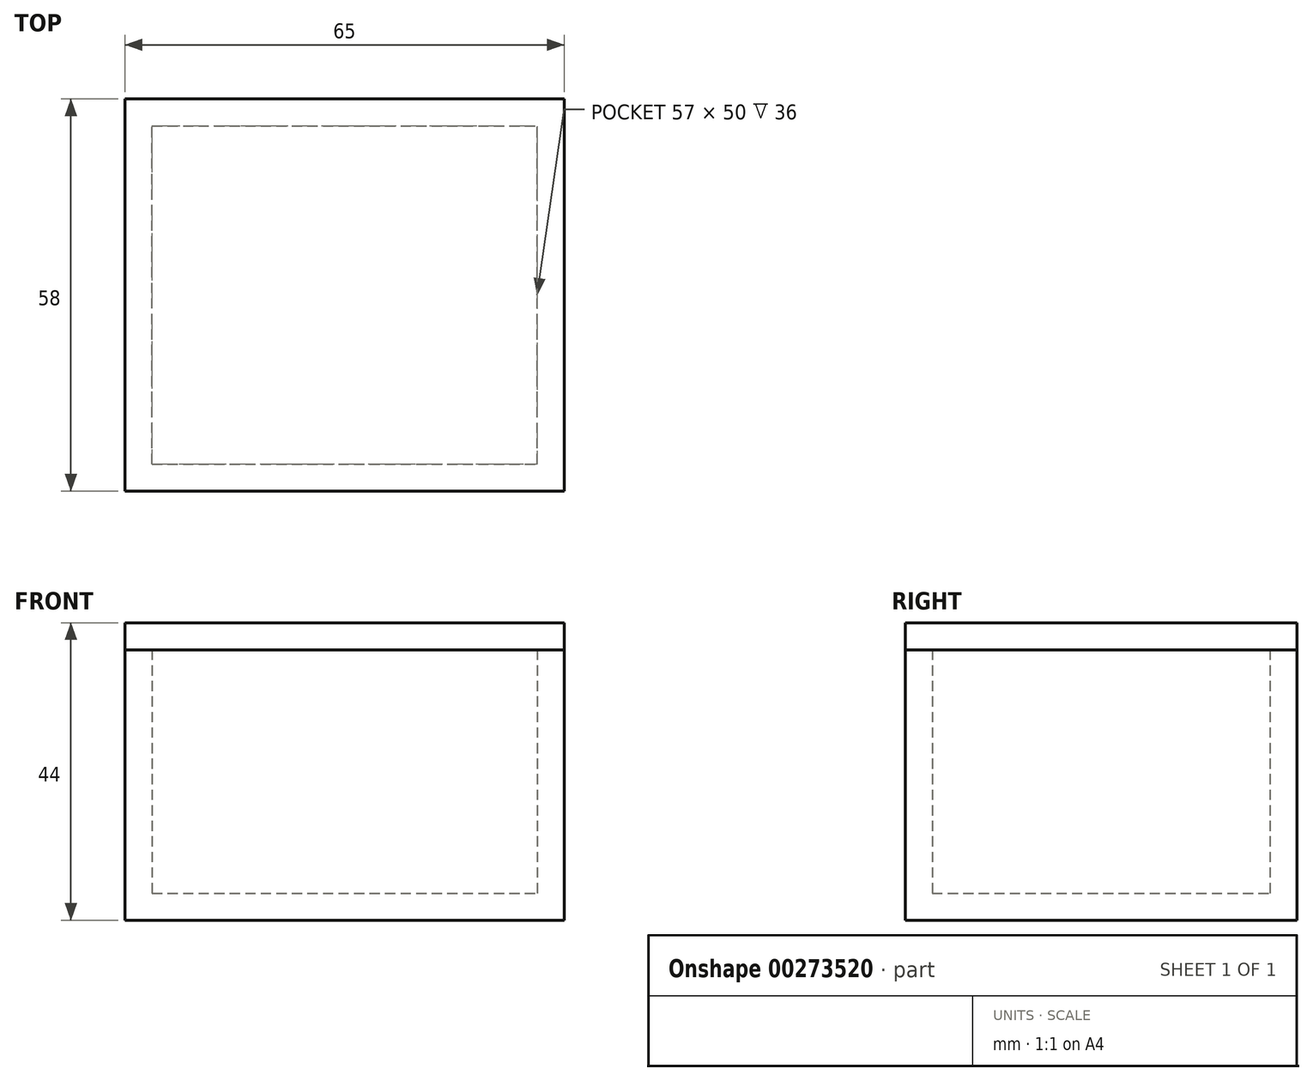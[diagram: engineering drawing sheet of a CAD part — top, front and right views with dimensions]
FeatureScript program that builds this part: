
annotation { "Feature Type Name" : "Feature", "Feature Type Description" : "" }
export const myFeature = defineFeature(function(context is Context, id is Id, definition is map)
    precondition{}
    {
        {
            var Q0;
            Q0=qCreatedBy(makeId("Top.planeOp"),FACE);
            var sketch = newSketch(context, id + "F0", { "sketchPlane" : qUnion([Q0])});
            skLineSegment(sketch, "E0.bottom", {"start": v(-32.5, -29) * mm, "end": v(32.5, -29) * mm});
            skLineSegment(sketch, "E0.top", {"start": v(-32.5, 29) * mm, "end": v(32.5, 29) * mm});
            skLineSegment(sketch, "E0.left", {"start": v(-32.5, -29) * mm, "end": v(-32.5, 29) * mm});
            skLineSegment(sketch, "E0.right", {"start": v(32.5, -29) * mm, "end": v(32.5, 29) * mm});
            skLineSegment(sketch, "E1", {"start": v(-32.5, -29) * mm, "end": v(32.5, 29) * mm, "construction": true});
            skLineSegment(sketch, "E2", {"start": v(32.5, -29) * mm, "end": v(-32.5, 29) * mm, "construction": true});
            skPoint(sketch, "E3", {"position": v(0, 0) * mm});
            skSolve(sketch);
        }
        {
            var Q0;
            Q0 = qSketchRegion(id + "F0", true);
            extrude(context, id + "F1", {"entities" : qUnion([Q0]), "depth" : 40 * mm});
        }
        {
            var Q0;
            Q0=makeQuery(id+"F1.opExtrude","CAP_FACE",FACE,{"disambiguationData":[OSD([sQuery(id+"F0.wireOp",EDGE,"E0.bottom"),sQuery(id+"F0.wireOp",EDGE,"E0.top"),sQuery(id+"F0.wireOp",EDGE,"E0.left"),sQuery(id+"F0.wireOp",EDGE,"E0.right")])],"isStart":false});
            shell(context, id + "F2", {"entities" : qUnion([Q0]), "thickness" : 4 * mm});
        }
        {
            var Q0;
            Q0=makeQuery(id+"F1.opExtrude","CAP_FACE",FACE,{"disambiguationData":[OSD([sQuery(id+"F0.wireOp",EDGE,"E0.bottom"),sQuery(id+"F0.wireOp",EDGE,"E0.top"),sQuery(id+"F0.wireOp",EDGE,"E0.left"),sQuery(id+"F0.wireOp",EDGE,"E0.right")])],"isStart":false});
            var sketch = newSketch(context, id + "F3", { "sketchPlane" : qUnion([Q0])});
            skLineSegment(sketch, "E4.0", {"start": v(-32.5, 29) * mm, "end": v(32.5, 29) * mm});
            skLineSegment(sketch, "E4.1", {"start": v(32.5, -29) * mm, "end": v(32.5, 29) * mm});
            skLineSegment(sketch, "E4.2", {"start": v(-32.5, -29) * mm, "end": v(32.5, -29) * mm});
            skLineSegment(sketch, "E4.3", {"start": v(-32.5, -29) * mm, "end": v(-32.5, 29) * mm});
            skSolve(sketch);
        }
        {
            var Q0;
            Q0 = qSketchRegion(id + "F3", true);
            extrude(context, id + "F4", {"entities" : qUnion([Q0]), "depth" : 4 * mm});
        }
    });
